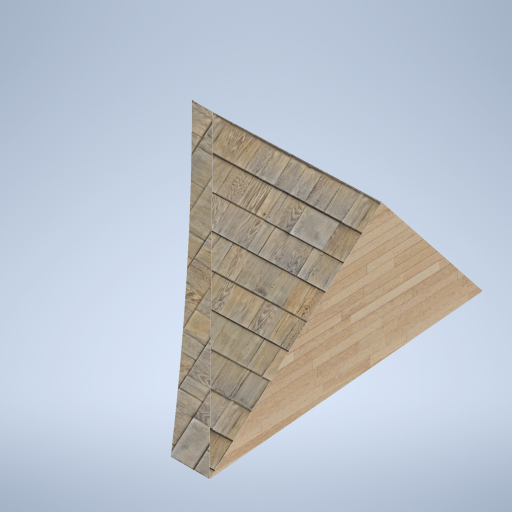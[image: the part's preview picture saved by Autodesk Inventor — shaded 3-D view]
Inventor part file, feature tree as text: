
AUTODESK INVENTOR PART (.ipt)
format: ipt  version: 2024.2 (Build 282272000, 272)  size: 423,936 bytes
history: native  units: in
note: dims shown in document units (in); Inventor stores cm internally (conversion verified against a paired STEP export)
features: sketch x6, plane x5, other x3
ambient origin geometry x8: Origin, YZ Plane, XZ Plane, XY Plane, X Axis, Y Axis, Z Axis, Center Point
bodies: Solid1 (feature_tree)
feature tree (14):
  other  "panel_pad_03_MIR.ipt"
  other  "Solid1::panel_pad_03_MIR.ipt"
  other  "TaggingFeature1"
  sketch  "Sketch1"  dims[d0=0.3937in]
  sketch  "Sketch2"
  sketch  "Sketch3"
  sketch  "Sketch6"
  sketch  "Sketch7"
  sketch  "Sketch8"
  plane  "Work Plane1"
  plane  "Work Plane2"
  plane  "Work Plane3"
  plane  "Work Plane4"
  plane  "Work Plane5"
